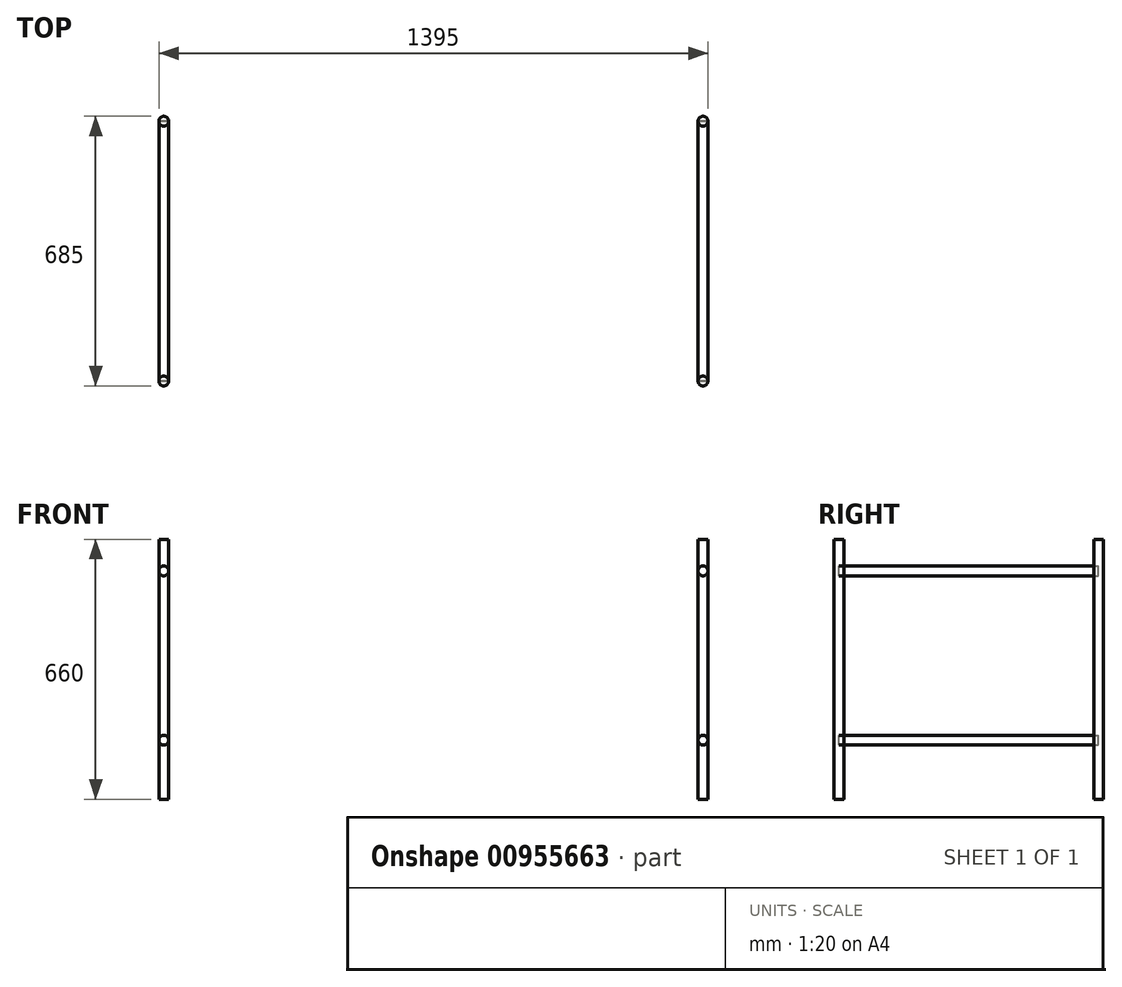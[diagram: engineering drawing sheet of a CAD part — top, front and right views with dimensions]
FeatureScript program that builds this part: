
annotation { "Feature Type Name" : "Feature", "Feature Type Description" : "" }
export const myFeature = defineFeature(function(context is Context, id is Id, definition is map)
    precondition{}
    {
        {
            var Q0;
            Q0=qCreatedBy(makeId("Top.planeOp"),FACE);
            var sketch = newSketch(context, id + "F0", { "sketchPlane" : qUnion([Q0])});
            skLineSegment(sketch, "E0.bottom", {"start": v(-685, -660) * mm, "end": v(685, -660) * mm, "construction": true});
            skLineSegment(sketch, "E0.top", {"start": v(-685, 0) * mm, "end": v(685, 0) * mm, "construction": true});
            skLineSegment(sketch, "E0.left", {"start": v(-685, -660) * mm, "end": v(-685, 0) * mm, "construction": true});
            skLineSegment(sketch, "E0.right", {"start": v(685, -660) * mm, "end": v(685, 0) * mm, "construction": true});
            skCircle(sketch, "E1", {"center": v(-685, 0) * mm, "radius": 12.5 * mm});
            skCircle(sketch, "E2", {"center": v(-685, -660) * mm, "radius": 12.5 * mm});
            skCircle(sketch, "E3", {"center": v(685, -660) * mm, "radius": 12.5 * mm});
            skCircle(sketch, "E4", {"center": v(685, 0) * mm, "radius": 12.5 * mm});
            skSolve(sketch);
        }
        {
            var Q0;
            Q0 = qSketchRegion(id + "F0", true);
            extrude(context, id + "F1", {"entities" : qUnion([Q0]), "depth" : 660 * mm, "offsetDistance" : 25 * mm});
        }
        {
            var Q0;
            Q0=qCreatedBy(makeId("Front.planeOp"),FACE);
            var sketch = newSketch(context, id + "F2", { "sketchPlane" : qUnion([Q0])});
            skLineSegment(sketch, "E5.bottom", {"start": v(-685, 0) * mm, "end": v(685, 0) * mm, "construction": true});
            skLineSegment(sketch, "E5.top", {"start": v(-685, 580) * mm, "end": v(685, 580) * mm, "construction": true});
            skLineSegment(sketch, "E5.left", {"start": v(-685, 0) * mm, "end": v(-685, 580) * mm, "construction": true});
            skLineSegment(sketch, "E5.right", {"start": v(685, 0) * mm, "end": v(685, 580) * mm, "construction": true});
            skLineSegment(sketch, "E6", {"start": v(-685, 150) * mm, "end": v(685, 150) * mm, "construction": true});
            skCircle(sketch, "E7", {"center": v(-685, 580) * mm, "radius": 12.5 * mm});
            skCircle(sketch, "E8", {"center": v(-685, 150) * mm, "radius": 12.5 * mm});
            skCircle(sketch, "E9", {"center": v(685, 580) * mm, "radius": 12.5 * mm});
            skCircle(sketch, "E10", {"center": v(685, 150) * mm, "radius": 12.5 * mm});
            skSolve(sketch);
        }
        {
            var Q0;
            Q0 = qSketchRegion(id + "F2", true);
            extrude(context, id + "F3", {"entities" : qUnion([Q0]), "depth" : 660 * mm, "offsetDistance" : 25 * mm});
        }
    });
